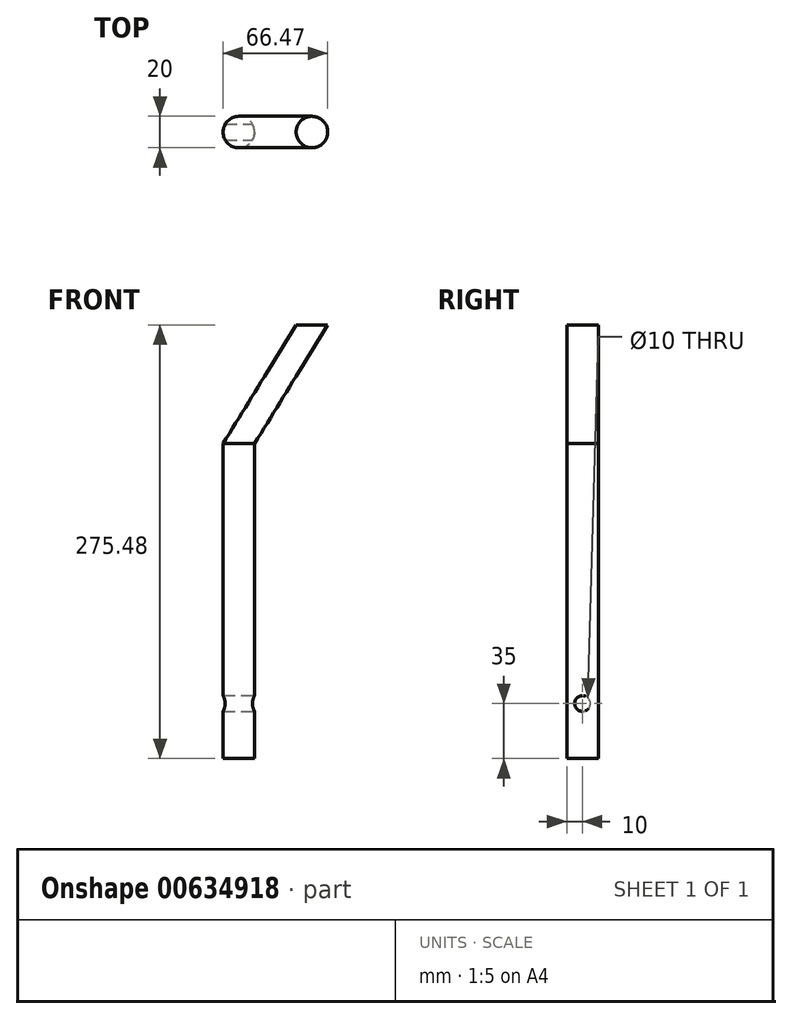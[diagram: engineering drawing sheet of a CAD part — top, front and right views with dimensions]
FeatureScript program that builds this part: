
annotation { "Feature Type Name" : "Feature", "Feature Type Description" : "" }
export const myFeature = defineFeature(function(context is Context, id is Id, definition is map)
    precondition{}
    {
        {
            var Q0;
            Q0=qCreatedBy(makeId("Top.planeOp"),FACE);
            var sketch = newSketch(context, id + "F0", { "sketchPlane" : qUnion([Q0])});
            skCircle(sketch, "E0", {"center": v(0, 0) * mm, "radius": 10 * mm});
            skSolve(sketch);
        }
        {
            var Q0;
            Q0 = qSketchRegion(id + "F0", true);
            extrude(context, id + "F1", {"entities" : qUnion([Q0]), "depth" : 200 * mm, "offsetDistance" : 25 * mm});
        }
        {
            var Q0;
            Q0=qCreatedBy(makeId("Right.planeOp"),FACE);
            var sketch = newSketch(context, id + "F2", { "sketchPlane" : qUnion([Q0])});
            skCircle(sketch, "E1", {"center": v(0, 35) * mm, "radius": 5 * mm});
            skSolve(sketch);
        }
        {
            var Q0;
            Q0 = qSketchRegion(id + "F2", true);
            extrude(context, id + "F3", {"entities" : qUnion([Q0]), "operationType" : NewBodyOperationType.REMOVE, "oppositeDirection" : true, "depth" : 25 * mm, "offsetDistance" : 25 * mm, "symmetric" : true});
        }
        {
            var Q0;
            Q0=qCreatedBy(makeId("Front.planeOp"),FACE);
            var sketch = newSketch(context, id + "F4", { "sketchPlane" : qUnion([Q0])});
            skLineSegment(sketch, "E2", {"start": v(0, 200) * mm, "end": v(46.47, 275.48) * mm});
            skSolve(sketch);
        }
        {
            var Q0;
            Q0=makeQuery(id+"F1.opExtrude","CAP_FACE",FACE,{"disambiguationData":[OSD([sQuery(id+"F0.wireOp",EDGE,"E0")])],"isStart":false});
            var Q1;
            Q1=sQuery(id+"F4.wireOp",EDGE,"E2");
            sweep(context, id + "F5", {"operationType" : NewBodyOperationType.ADD, "profiles" : qUnion([Q0]), "path" : qUnion([Q1])});
        }
    });
